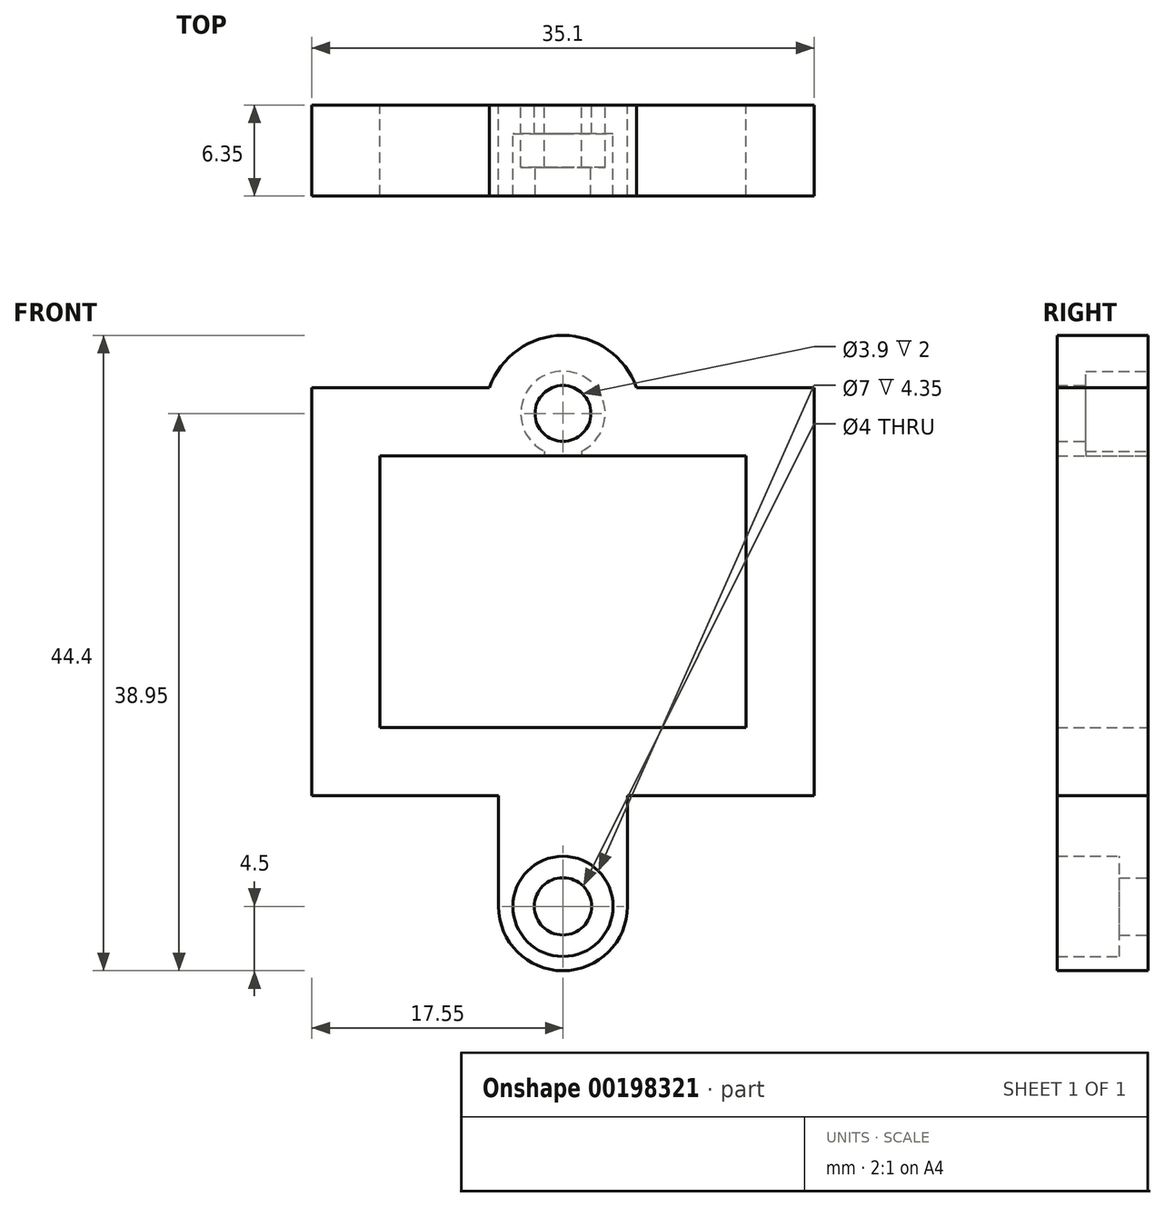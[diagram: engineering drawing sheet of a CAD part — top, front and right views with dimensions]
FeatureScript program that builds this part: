
annotation { "Feature Type Name" : "Feature", "Feature Type Description" : "" }
export const myFeature = defineFeature(function(context is Context, id is Id, definition is map)
    precondition{}
    {
        {
            var Q0;
            Q0=qCreatedBy(makeId("Front.planeOp"),FACE);
            var sketch = newSketch(context, id + "F0", { "sketchPlane" : qUnion([Q0])});
            skLineSegment(sketch, "E0.bottom", {"start": v(-12.65, 9.35) * mm, "end": v(12.65, 9.35) * mm, "construction": true});
            skLineSegment(sketch, "E0.top", {"start": v(-12.65, -9.35) * mm, "end": v(12.65, -9.35) * mm, "construction": true});
            skLineSegment(sketch, "E0.left", {"start": v(-12.65, 9.35) * mm, "end": v(-12.65, -9.35) * mm, "construction": true});
            skLineSegment(sketch, "E0.right", {"start": v(12.65, 9.35) * mm, "end": v(12.65, -9.35) * mm, "construction": true});
            skLineSegment(sketch, "E1", {"start": v(-12.65, 9.35) * mm, "end": v(12.65, -9.35) * mm, "construction": true});
            skLineSegment(sketch, "E2", {"start": v(12.65, 9.35) * mm, "end": v(-12.65, -9.35) * mm, "construction": true});
            skPoint(sketch, "E3", {"position": v(0, 0) * mm});
            skLineSegment(sketch, "E4.0", {"start": v(-12.8, 9.5) * mm, "end": v(12.8, 9.5) * mm});
            skLineSegment(sketch, "E4.1", {"start": v(-12.8, 9.5) * mm, "end": v(-12.8, -9.5) * mm});
            skLineSegment(sketch, "E4.2", {"start": v(-12.8, -9.5) * mm, "end": v(12.8, -9.5) * mm});
            skLineSegment(sketch, "E4.3", {"start": v(12.8, 9.5) * mm, "end": v(12.8, -9.5) * mm});
            skLineSegment(sketch, "E5.bottom", {"start": v(-7.05, 3.15) * mm, "end": v(-5.55, 3.15) * mm});
            skLineSegment(sketch, "E5.top", {"start": v(-7.05, -3.15) * mm, "end": v(-5.55, -3.15) * mm});
            skLineSegment(sketch, "E5.left", {"start": v(-7.05, 3.15) * mm, "end": v(-7.05, -3.15) * mm});
            skLineSegment(sketch, "E5.right", {"start": v(-5.55, 3.15) * mm, "end": v(-5.55, -3.15) * mm});
            skLineSegment(sketch, "E6.bottom", {"start": v(5.55, 4) * mm, "end": v(7.05, 4) * mm});
            skLineSegment(sketch, "E6.top", {"start": v(5.55, -4) * mm, "end": v(7.05, -4) * mm});
            skLineSegment(sketch, "E6.left", {"start": v(5.55, 4) * mm, "end": v(5.55, -4) * mm});
            skLineSegment(sketch, "E6.right", {"start": v(7.05, 4) * mm, "end": v(7.05, -4) * mm});
            skPoint(sketch, "E7", {"position": v(-5.55, 0) * mm});
            skPoint(sketch, "E8", {"position": v(5.55, 0) * mm});
            skLineSegment(sketch, "E9.0", {"start": v(-17.55, 14.25) * mm, "end": v(17.55, 14.25) * mm});
            skLineSegment(sketch, "E9.1", {"start": v(-17.55, 14.25) * mm, "end": v(-17.55, -14.25) * mm});
            skLineSegment(sketch, "E9.2", {"start": v(-17.55, -14.25) * mm, "end": v(17.55, -14.25) * mm});
            skLineSegment(sketch, "E9.3", {"start": v(17.55, 14.25) * mm, "end": v(17.55, -14.25) * mm});
            skCircle(sketch, "E10", {"center": v(0, 12.45) * mm, "radius": 2.95 * mm});
            skPoint(sketch, "E10.centerSnap0", {"position": v(0, 9.5) * mm});
            skCircle(sketch, "E11", {"center": v(0, 12.45) * mm, "radius": 1.95 * mm});
            skArc(sketch, "E12.trimOffspring", {"start": v(5.14, 14.25) * mm, "mid": v(0, 17.9) * mm, "end": v(-5.14, 14.25) * mm});
            skCircle(sketch, "E13", {"center": v(0, -22) * mm, "radius": 3.5 * mm});
            skArc(sketch, "E14.0", {"start": v(-4.5, -22) * mm, "mid": v(0, -26.5) * mm, "end": v(4.5, -22) * mm});
            skLineSegment(sketch, "E15", {"start": v(4.5, -22) * mm, "end": v(4.5, -14.25) * mm});
            skLineSegment(sketch, "E16", {"start": v(-4.5, -22) * mm, "end": v(-4.5, -14.25) * mm});
            skCircle(sketch, "E17", {"center": v(0, -22) * mm, "radius": 2 * mm});
            skSolve(sketch);
        }
        {
            var Q0;
            {var subQ14=sQuery(id+"F0.wireOp",EDGE,"E4.1");Q0=makeQuery(id+"F0.imprint","IMPRINT",FACE,{"disambiguationData":[TD([[makeQuery(id+"F0.imprint","IMPRINT",EDGE,{"derivedFrom":subQ14}),-1.0]])]});}
            var Q1;
            {var subQ0=sQuery(id+"F0.wireOp",EDGE,"E10");var subQ2=sQuery(id+"F0.wireOp",EDGE,"E9.0");var subQ3=makeQuery(id+"F0.imprint","INTERSECT",VERTEX,{"disambiguationData":[OD(0.0)],"derivedFrom":[subQ2,subQ0]});Q1=makeQuery(id+"F0.imprint","IMPRINT",FACE,{"disambiguationData":[TD([[makeQuery(id+"F0.imprint","IMPRINT",EDGE,{"disambiguationData":[TD([[subQ3,-1.0]])],"derivedFrom":subQ2}),-1.0]])]});}
            var Q2;
            {var subQ0=sQuery(id+"F0.wireOp",EDGE,"E12.trimOffspring");Q2=makeQuery(id+"F0.imprint","IMPRINT",FACE,{"disambiguationData":[TD([[makeQuery(id+"F0.imprint","IMPRINT",EDGE,{"derivedFrom":subQ0}),1.0]])]});}
            var Q3;
            {var subQ0=sQuery(id+"F0.wireOp",EDGE,"E10");var subQ1=sQuery(id+"F0.wireOp",EDGE,"E9.0");var subQ2=makeQuery(id+"F0.imprint","INTERSECT",VERTEX,{"disambiguationData":[OD(0.0)],"derivedFrom":[subQ1,subQ0]});Q3=makeQuery(id+"F0.imprint","IMPRINT",FACE,{"disambiguationData":[TD([[makeQuery(id+"F0.imprint","IMPRINT",EDGE,{"disambiguationData":[TD([[subQ2,-1.0]])],"derivedFrom":subQ1}),1.0]])]});}
            var Q4;
            Q4=makeQuery(id+"F0.imprint","IMPRINT",FACE,{"disambiguationData":[TD([[makeQuery(id+"F0.imprint","IMPRINT",EDGE,{"derivedFrom":sQuery(id+"F0.wireOp",EDGE,"E13")}),-1.0]])]});
            extrude(context, id + "F1", {"entities" : qUnion([Q0, Q1, Q2, Q3, Q4]), "depth" : 6.35 * mm});
        }
        {
            var Q0;
            Q0=makeQuery(id+"F0.imprint","IMPRINT",FACE,{"disambiguationData":[TD([[makeQuery(id+"F0.imprint","IMPRINT",EDGE,{"derivedFrom":sQuery(id+"F0.wireOp",EDGE,"E13")}),1.0]])]});
            extrude(context, id + "F2", {"entities" : qUnion([Q0]), "operationType" : NewBodyOperationType.ADD, "depth" : 2 * mm});
        }
        {
            var Q0;
            {var subQ14=sQuery(id+"F0.wireOp",EDGE,"E4.1");Q0=makeQuery(id+"F0.imprint","IMPRINT",FACE,{"disambiguationData":[TD([[makeQuery(id+"F0.imprint","IMPRINT",EDGE,{"derivedFrom":subQ14}),-1.0]])]});}
            var sketch = newSketch(context, id + "F3", { "sketchPlane" : qUnion([Q0])});
            skCircle(sketch, "E18.0", {"center": v(0, 12.45) * mm, "radius": 2.95 * mm});
            skLineSegment(sketch, "E19.0", {"start": v(-12.8, 9.5) * mm, "end": v(12.8, 9.5) * mm});
            skLineSegment(sketch, "E20", {"start": v(1.31, 9.8) * mm, "end": v(1.31, 9.5) * mm});
            skLineSegment(sketch, "E21", {"start": v(-1.31, 9.8) * mm, "end": v(-1.31, 9.5) * mm});
            skLineSegment(sketch, "E22", {"start": v(-1.31, 9.5) * mm, "end": v(1.31, 9.5) * mm});
            skSolve(sketch);
        }
        {
            var Q0;
            {var subQ0=sQuery(id+"F0.wireOp",EDGE,"E10");var subQ2=sQuery(id+"F0.wireOp",EDGE,"E9.0");var subQ3=makeQuery(id+"F0.imprint","INTERSECT",VERTEX,{"disambiguationData":[OD(0.0)],"derivedFrom":[subQ2,subQ0]});Q0=makeQuery(id+"F0.imprint","IMPRINT",FACE,{"disambiguationData":[TD([[makeQuery(id+"F0.imprint","IMPRINT",EDGE,{"disambiguationData":[TD([[subQ3,-1.0]])],"derivedFrom":subQ2}),-1.0]])]});}
            var Q1;
            {var subQ0=sQuery(id+"F0.wireOp",EDGE,"E10");var subQ1=sQuery(id+"F0.wireOp",EDGE,"E9.0");var subQ2=makeQuery(id+"F0.imprint","INTERSECT",VERTEX,{"disambiguationData":[OD(0.0)],"derivedFrom":[subQ1,subQ0]});Q1=makeQuery(id+"F0.imprint","IMPRINT",FACE,{"disambiguationData":[TD([[makeQuery(id+"F0.imprint","IMPRINT",EDGE,{"disambiguationData":[TD([[subQ2,-1.0]])],"derivedFrom":subQ1}),1.0]])]});}
            var Q2;
            {var subQ3=sQuery(id+"F3.wireOp",EDGE,"E21");Q2=makeQuery(id+"F3.imprint","IMPRINT",FACE,{"disambiguationData":[TD([[makeQuery(id+"F3.imprint","IMPRINT",EDGE,{"derivedFrom":subQ3}),1.0]])]});}
            var Q3;
            {var subQ3=sQuery(id+"F3.wireOp",EDGE,"E20");Q3=makeQuery(id+"F3.imprint","IMPRINT",FACE,{"disambiguationData":[TD([[makeQuery(id+"F3.imprint","IMPRINT",EDGE,{"derivedFrom":subQ3}),-1.0]])]});}
            extrude(context, id + "F4", {"entities" : qUnion([Q0, Q1, Q2, Q3]), "operationType" : NewBodyOperationType.REMOVE, "depth" : (6.35 - 2) * mm});
        }
    });
